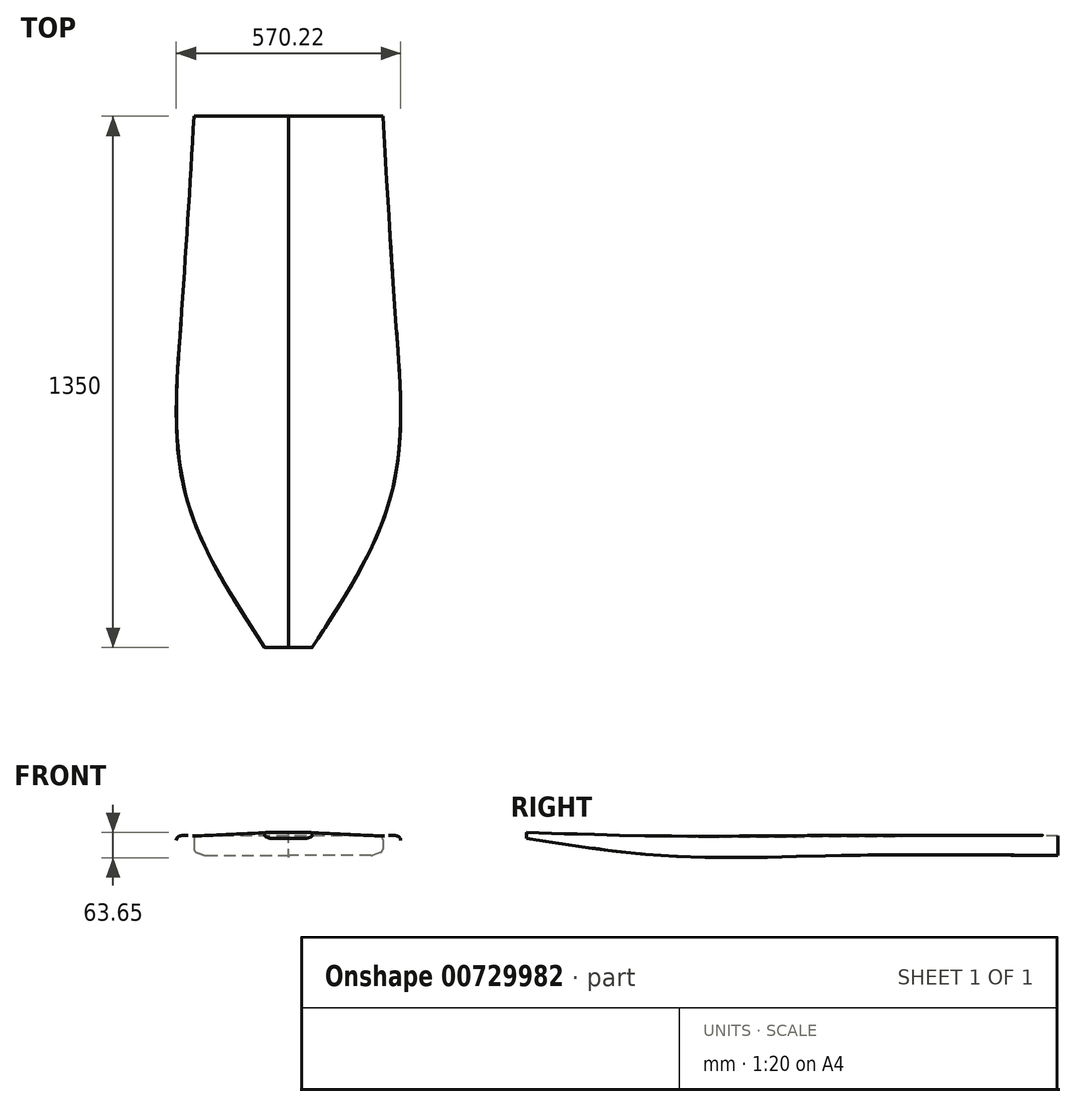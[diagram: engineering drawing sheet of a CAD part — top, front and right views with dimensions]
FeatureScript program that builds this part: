
annotation { "Feature Type Name" : "Feature", "Feature Type Description" : "" }
export const myFeature = defineFeature(function(context is Context, id is Id, definition is map)
    precondition{}
    {
        {
            var Q0;
            Q0=qCreatedBy(makeId("Front.planeOp"),FACE);
            var sketch = newSketch(context, id + "F0", { "sketchPlane" : qUnion([Q0])});
            skLineSegment(sketch, "E0.bottom", {"start": v(230, 25) * mm, "end": v(0, 25) * mm});
            skLineSegment(sketch, "E0.right", {"start": v(0, 25) * mm, "end": v(0, -25) * mm});
            skPoint(sketch, "E0.middle", {"position": v(0, 0) * mm});
            skPoint(sketch, "E1", {"position": v(240, -14.72) * mm});
            skLineSegment(sketch, "E2", {"start": v(233.42, -17.12) * mm, "end": v(213.42, -24.4) * mm});
            skLineSegment(sketch, "E3", {"start": v(240, 15) * mm, "end": v(240, -7.72) * mm});
            skLineSegment(sketch, "E4", {"start": v(210, -25) * mm, "end": v(0, -25) * mm});
            skPoint(sketch, "E5.visualSharp", {"position": v(240, 25) * mm});
            skArc(sketch, "E5.filletArc", {"start": v(240, 15) * mm, "mid": v(237.07, 22.07) * mm, "end": v(230, 25) * mm});
            skArc(sketch, "E6.filletArc", {"start": v(233.42, -17.12) * mm, "mid": v(238.2, -13.46) * mm, "end": v(240, -7.72) * mm});
            skPoint(sketch, "E7.visualSharp", {"position": v(211.76, -25) * mm});
            skArc(sketch, "E7.filletArc", {"start": v(210, -25) * mm, "mid": v(211.74, -24.85) * mm, "end": v(213.42, -24.4) * mm});
            skSolve(sketch);
        }
        {
            var Q0;
            Q0=qCreatedBy(makeId("Front.planeOp"),FACE);
            cPlane(context, id + "F1", {"entities" : qUnion([Q0]), "cplaneType" : CPlaneType.OFFSET, "offset" : 550 * mm, "width" : 150 * mm, "height" : 150 * mm});
        }
        {
            var Q0;
            Q0=qCreatedBy(id+"F1.planeOp",FACE);
            var sketch = newSketch(context, id + "F2", { "sketchPlane" : qUnion([Q0])});
            skPoint(sketch, "E8.middle", {"position": v(0, 0.13) * mm});
            skPoint(sketch, "E9", {"position": v(275, -7.3) * mm});
            skLineSegment(sketch, "E10", {"start": v(268.42, -9.7) * mm, "end": v(228.42, -24.26) * mm});
            skLineSegment(sketch, "E11", {"start": v(275, 16.39) * mm, "end": v(275, -0.3) * mm});
            skLineSegment(sketch, "E12", {"start": v(225, -24.87) * mm, "end": v(0, -24.87) * mm});
            skPoint(sketch, "E13.visualSharp", {"position": v(275, 26.44) * mm});
            skArc(sketch, "E13.filletArc", {"start": v(275, 16.39) * mm, "mid": v(272.05, 23.47) * mm, "end": v(264.95, 26.39) * mm});
            skArc(sketch, "E14.filletArc", {"start": v(268.42, -9.7) * mm, "mid": v(273.2, -6.04) * mm, "end": v(275, -0.3) * mm});
            skPoint(sketch, "E15.visualSharp", {"position": v(226.76, -24.87) * mm});
            skArc(sketch, "E15.filletArc", {"start": v(225, -24.87) * mm, "mid": v(226.74, -24.71) * mm, "end": v(228.42, -24.26) * mm});
            skFitSpline(sketch, "E16", {"points": [v(264.95, 26.39) * mm, v(0, 22.13) * mm], "startDerivative": vector(-199.24, -1.04) * mm, "endDerivative": vector(-241.1, 2.73) * mm});
            skLineSegment(sketch, "E17", {"start": v(0, 22.13) * mm, "end": v(0, -24.87) * mm});
            skSolve(sketch);
        }
        {
            var Q0;
            Q0=qCreatedBy(makeId("Front.planeOp"),FACE);
            cPlane(context, id + "F3", {"entities" : qUnion([Q0]), "cplaneType" : CPlaneType.OFFSET, "offset" : 1000 * mm, "width" : 150 * mm, "height" : 150 * mm});
        }
        {
            var Q0;
            Q0=qCreatedBy(id+"F3.planeOp",FACE);
            var sketch = newSketch(context, id + "F4", { "sketchPlane" : qUnion([Q0])});
            skPoint(sketch, "E18.middle", {"position": v(0, -0.2) * mm});
            skPoint(sketch, "E19", {"position": v(250, -7.7) * mm});
            skLineSegment(sketch, "E20", {"start": v(243.43, -10.09) * mm, "end": v(203.56, -24.6) * mm});
            skLineSegment(sketch, "E21", {"start": v(250, 14.8) * mm, "end": v(250, -0.69) * mm});
            skPoint(sketch, "E22.visualSharp", {"position": v(250, 24.8) * mm});
            skArc(sketch, "E22.filletArc", {"start": v(250, 14.8) * mm, "mid": v(247.13, 21.83) * mm, "end": v(240.14, 24.8) * mm});
            skArc(sketch, "E23.filletArc", {"start": v(243.43, -10.09) * mm, "mid": v(248.2, -6.42) * mm, "end": v(250, -0.69) * mm});
            skPoint(sketch, "E24.visualSharp", {"position": v(201.9, -25.2) * mm});
            skArc(sketch, "E24.filletArc", {"start": v(200.14, -25.2) * mm, "mid": v(201.88, -25.05) * mm, "end": v(203.56, -24.6) * mm});
            skFitSpline(sketch, "E25", {"points": [v(0, -24.35) * mm, v(200.14, -25.2) * mm], "startDerivative": vector(199.15, 4.07) * mm, "endDerivative": vector(199.97, 0) * mm});
            skFitSpline(sketch, "E26", {"points": [v(240.14, 24.8) * mm, v(0, 22.65) * mm], "startDerivative": vector(-181.94, -7.35) * mm, "endDerivative": vector(-232.53, 1.78) * mm});
            skLineSegment(sketch, "E27", {"start": v(0, 22.65) * mm, "end": v(0, -24.35) * mm});
            skSolve(sketch);
        }
        {
            var Q0;
            Q0=qCreatedBy(makeId("Front.planeOp"),FACE);
            cPlane(context, id + "F5", {"entities" : qUnion([Q0]), "cplaneType" : CPlaneType.OFFSET, "offset" : 1350 * mm, "width" : 150 * mm, "height" : 150 * mm});
        }
        {
            var Q0;
            Q0=qCreatedBy(id+"F5.planeOp",FACE);
            var sketch = newSketch(context, id + "F6", { "sketchPlane" : qUnion([Q0])});
            skLineSegment(sketch, "E28.bottom", {"start": v(57, 33.43) * mm, "end": v(0, 33.43) * mm});
            skLineSegment(sketch, "E28.right", {"start": v(0, 33.43) * mm, "end": v(0, 18.43) * mm});
            skPoint(sketch, "E28.middle", {"position": v(190.18, -17.57) * mm});
            skPoint(sketch, "E29", {"position": v(60, 23.7) * mm});
            skLineSegment(sketch, "E30", {"start": v(58.03, 22.98) * mm, "end": v(46.03, 18.61) * mm});
            skLineSegment(sketch, "E31", {"start": v(60, 30.43) * mm, "end": v(60, 25.8) * mm});
            skLineSegment(sketch, "E32", {"start": v(45, 18.43) * mm, "end": v(0, 18.43) * mm});
            skPoint(sketch, "E33.visualSharp", {"position": v(60, 33.43) * mm});
            skArc(sketch, "E33.filletArc", {"start": v(60, 30.43) * mm, "mid": v(59.12, 32.55) * mm, "end": v(57, 33.43) * mm});
            skArc(sketch, "E34.filletArc", {"start": v(58.03, 22.98) * mm, "mid": v(59.46, 24.08) * mm, "end": v(60, 25.8) * mm});
            skPoint(sketch, "E35.visualSharp", {"position": v(45.53, 18.43) * mm});
            skArc(sketch, "E35.filletArc", {"start": v(45, 18.43) * mm, "mid": v(45.52, 18.48) * mm, "end": v(46.03, 18.61) * mm});
            skSolve(sketch);
        }
        {
            var Q0;
            Q0=makeQuery(id+"F0.imprint","IMPRINT",FACE,{"disambiguationData":[TD([[makeQuery(id+"F0.imprint","IMPRINT",EDGE,{"derivedFrom":sQuery(id+"F0.wireOp",EDGE,"E0.bottom")}),1.0]])]});
            var Q1;
            Q1=makeQuery(id+"F2.imprint","IMPRINT",FACE,{"disambiguationData":[TD([[makeQuery(id+"F2.imprint","IMPRINT",EDGE,{"derivedFrom":sQuery(id+"F2.wireOp",EDGE,"E10")}),-1.0]])]});
            var Q2;
            Q2=makeQuery(id+"F4.imprint","IMPRINT",FACE,{"disambiguationData":[TD([[makeQuery(id+"F4.imprint","IMPRINT",EDGE,{"derivedFrom":sQuery(id+"F4.wireOp",EDGE,"E20")}),-1.0]])]});
            var Q3;
            Q3=makeQuery(id+"F6.imprint","IMPRINT",FACE,{"disambiguationData":[TD([[makeQuery(id+"F6.imprint","IMPRINT",EDGE,{"derivedFrom":sQuery(id+"F6.wireOp",EDGE,"E28.bottom")}),1.0]])]});
            loft(context, id + "F7", {"sheetProfilesArray" : [{ "sheetProfileEntities" : qUnion([Q0]) }, { "sheetProfileEntities" : qUnion([Q1]) }, { "sheetProfileEntities" : qUnion([Q2]) }, { "sheetProfileEntities" : qUnion([Q3]) }]});
        }
        {
            var Q0;
            Q0=makeQuery(id+"F7.opLoft","SWEPT_BODY",BODY,{"disambiguationData":[OSD([makeQuery(id+"F0.imprint","IMPRINT",FACE,{"disambiguationData":[TD([[makeQuery(id+"F0.imprint","IMPRINT",EDGE,{"derivedFrom":sQuery(id+"F0.wireOp",EDGE,"E0.bottom")}),1.0]])]}),sQuery(id+"F2.wireOp",EDGE,"E11"),sQuery(id+"F4.wireOp",EDGE,"E22.filletArc"),makeQuery(id+"F6.imprint","IMPRINT",FACE,{"disambiguationData":[TD([[makeQuery(id+"F6.imprint","IMPRINT",EDGE,{"derivedFrom":sQuery(id+"F6.wireOp",EDGE,"E28.bottom")}),1.0]])]})])]});
            var Q1;
            Q1=qCreatedBy(makeId("Right.planeOp"),FACE);
            mirror(context, id + "F8", {"operationType" : NewBodyOperationType.ADD, "entities" : qUnion([Q0]), "mirrorPlane" : qUnion([Q1])});
        }
    });
